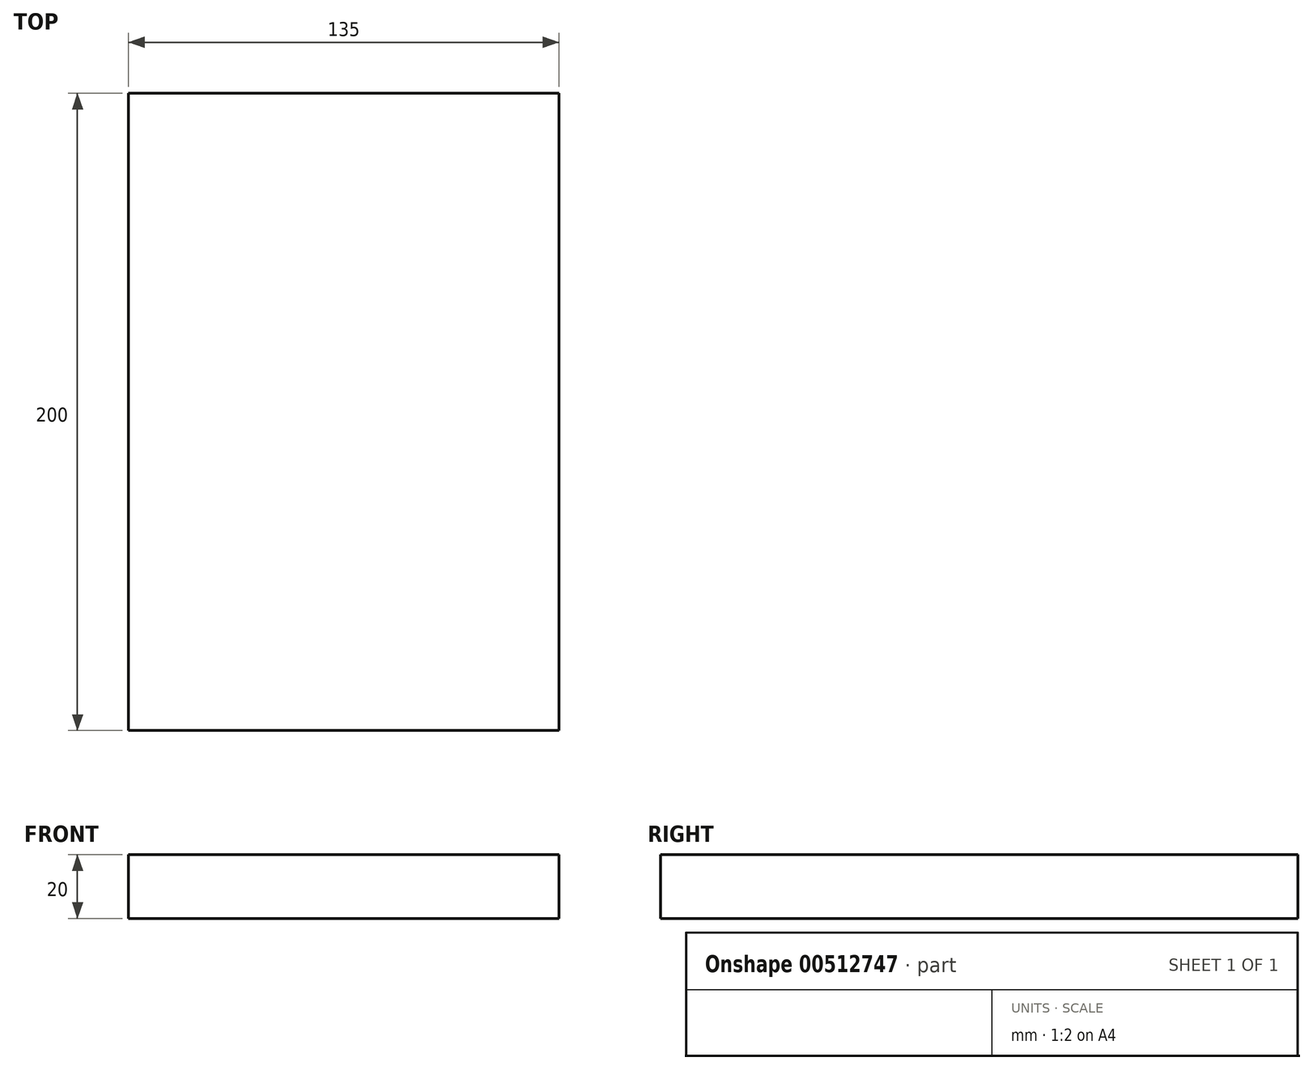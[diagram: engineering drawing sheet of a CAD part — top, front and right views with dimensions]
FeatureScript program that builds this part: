
annotation { "Feature Type Name" : "Feature", "Feature Type Description" : "" }
export const myFeature = defineFeature(function(context is Context, id is Id, definition is map)
    precondition{}
    {
        {
            var Q0;
            Q0=qCreatedBy(makeId("Top.planeOp"),FACE);
            var sketch = newSketch(context, id + "F0", { "sketchPlane" : qUnion([Q0])});
            skLineSegment(sketch, "E0.bottom", {"start": v(67.5, -100) * mm, "end": v(-67.5, -100) * mm});
            skLineSegment(sketch, "E0.top", {"start": v(67.5, 100) * mm, "end": v(-67.5, 100) * mm});
            skLineSegment(sketch, "E0.left", {"start": v(67.5, -100) * mm, "end": v(67.5, 100) * mm});
            skLineSegment(sketch, "E0.right", {"start": v(-67.5, -100) * mm, "end": v(-67.5, 100) * mm});
            skPoint(sketch, "E0.middle", {"position": v(0, 0) * mm});
            skSolve(sketch);
        }
        {
            var Q0;
            Q0 = qSketchRegion(id + "F0", true);
            extrude(context, id + "F1", {"entities" : qUnion([Q0]), "depth" : 20 * mm});
        }
    });
